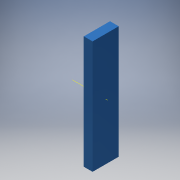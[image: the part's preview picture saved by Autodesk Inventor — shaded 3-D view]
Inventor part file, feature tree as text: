
AUTODESK INVENTOR PART (.ipt)
format: ipt  version: 2017 (Build 210142000, 142)  size: 108,032 bytes
history: native  units: mm
features: sketch x3, extrude x2, chamfer x1, other x1
ambient origin geometry x8: Origin, YZ Plane, XZ Plane, XY Plane, X Axis, Y Axis, Z Axis, Center Point
bodies: Solid1 (feature_tree)
feature tree (7):
  extrude  "Extrusion1"  Depth=41.6mm
  extrude  "Extrusion2"  Depth=3.22mm
  chamfer  "Chamfer1"  Distance=1.52mm
  sketch  "Sketch3"  dims[d5=1.0mm d6=1.52mm d7=0.0mm d8=1.52mm d9=2.0mm d10=45.0deg]
  other  "Work Axis1"
  sketch  "Sketch1"  dims[d0=9.65mm d1=41.6mm]
  sketch  "Sketch2"  dims[d2=3.22mm d3=0.0mm d4=29.1mm]
